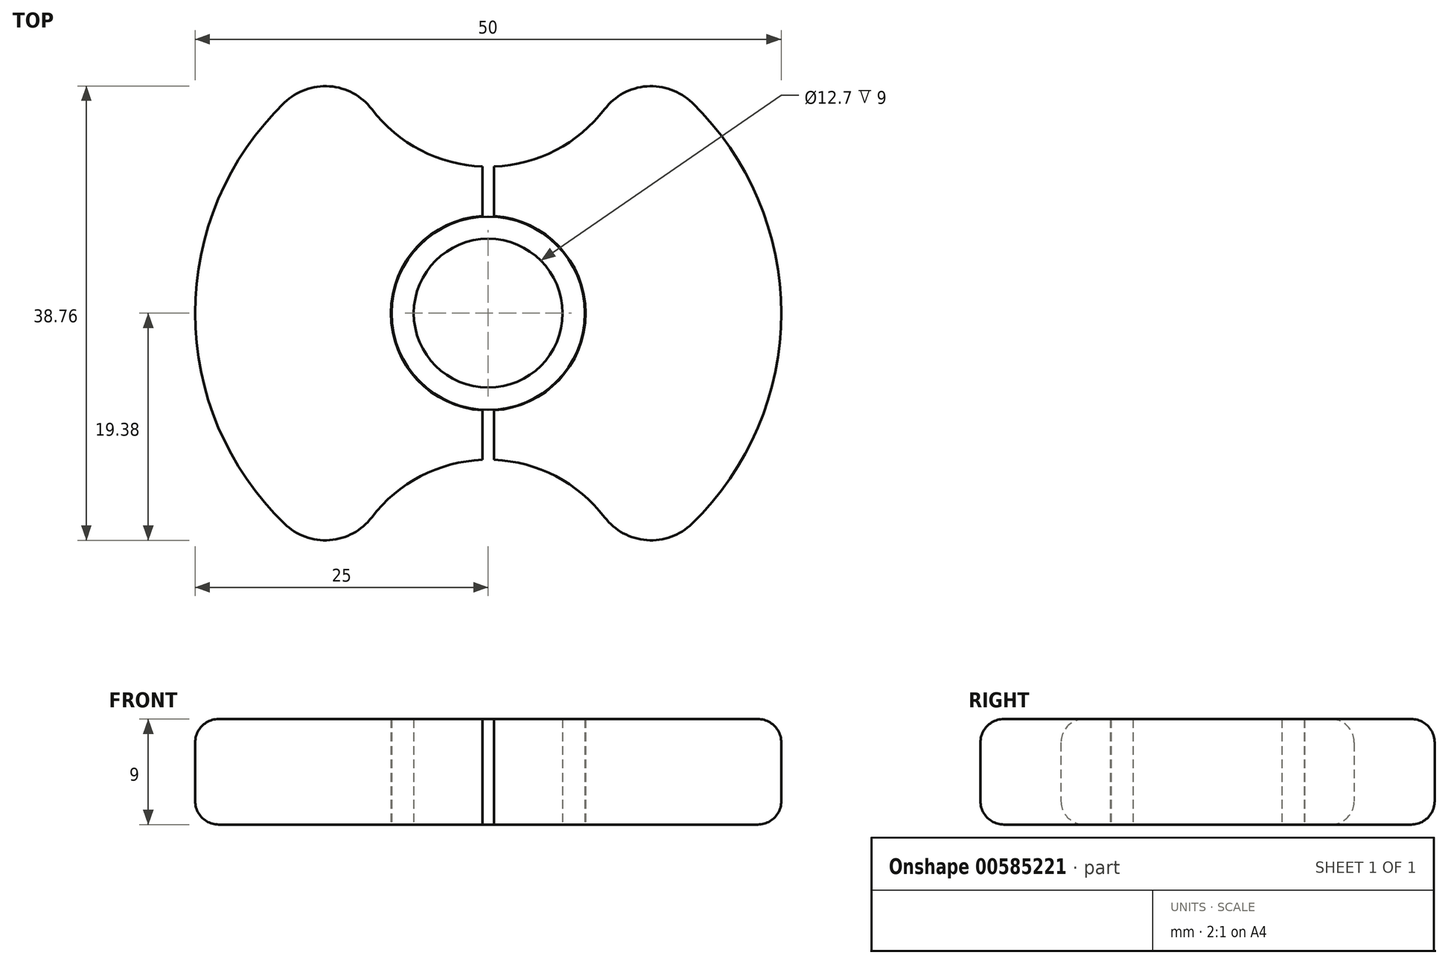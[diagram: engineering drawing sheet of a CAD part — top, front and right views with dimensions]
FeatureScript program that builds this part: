
annotation { "Feature Type Name" : "Feature", "Feature Type Description" : "" }
export const myFeature = defineFeature(function(context is Context, id is Id, definition is map)
    precondition{}
    {
        {
            var Q0;
            Q0=qCreatedBy(makeId("Top.planeOp"),FACE);
            var sketch = newSketch(context, id + "F0", { "sketchPlane" : qUnion([Q0])});
            skCircle(sketch, "E0", {"center": v(0, 0) * mm, "radius": 6.35 * mm});
            skArc(sketch, "E1", {"start": v(-12.1, 21.87) * mm, "mid": v(-25, 0) * mm, "end": v(-12.1, -21.88) * mm});
            skCircle(sketch, "E2", {"center": v(0, 0) * mm, "radius": 8.25 * mm});
            skArc(sketch, "E3", {"start": v(-12.1, 21.88) * mm, "mid": v(-7.85, 15.27) * mm, "end": v(-0.5, 12.51) * mm});
            skArc(sketch, "E4", {"start": v(12.1, -21.88) * mm, "mid": v(7.85, -15.27) * mm, "end": v(0.5, -12.51) * mm});
            skArc(sketch, "E5.trimOffspring", {"start": v(12.1, -21.88) * mm, "mid": v(25, 0) * mm, "end": v(12.1, 21.88) * mm});
            skArc(sketch, "E6", {"start": v(-0.5, 8.28) * mm, "mid": v(-8.3, 0) * mm, "end": v(-0.5, -8.28) * mm});
            skLineSegment(sketch, "E7.left", {"start": v(-0.5, -12.51) * mm, "end": v(-0.5, -8.28) * mm});
            skLineSegment(sketch, "E7.right", {"start": v(0.5, -12.51) * mm, "end": v(0.5, -8.28) * mm});
            skPoint(sketch, "E8.orphan", {"position": v(-0.5, 17.5) * mm});
            skPoint(sketch, "E9.orphan", {"position": v(0.5, 17.5) * mm});
            skArc(sketch, "E10.trimOffspring", {"start": v(0.5, 12.51) * mm, "mid": v(7.85, 15.27) * mm, "end": v(12.1, 21.88) * mm});
            skLineSegment(sketch, "E11.trimOffspring", {"start": v(0.5, 8.28) * mm, "end": v(0.5, 12.51) * mm});
            skLineSegment(sketch, "E12.trimOffspring", {"start": v(-0.5, 8.28) * mm, "end": v(-0.5, 12.51) * mm});
            skPoint(sketch, "E13.orphan", {"position": v(0.5, -17.5) * mm});
            skPoint(sketch, "E14.orphan", {"position": v(-0.5, -17.5) * mm});
            skArc(sketch, "E15.trimOffspring", {"start": v(-0.5, -12.51) * mm, "mid": v(-7.85, -15.27) * mm, "end": v(-12.1, -21.88) * mm});
            skArc(sketch, "E16.trimOffspring", {"start": v(0.5, -8.28) * mm, "mid": v(8.3, 0) * mm, "end": v(0.5, 8.28) * mm});
            skSolve(sketch);
        }
        {
            var Q0;
            Q0=makeQuery(id+"F0.imprint","IMPRINT",FACE,{"disambiguationData":[TD([[makeQuery(id+"F0.imprint","IMPRINT",EDGE,{"derivedFrom":sQuery(id+"F0.wireOp",EDGE,"E4")}),-1.0]])]});
            var Q1;
            Q1=makeQuery(id+"F0.imprint","IMPRINT",FACE,{"disambiguationData":[TD([[makeQuery(id+"F0.imprint","IMPRINT",EDGE,{"derivedFrom":sQuery(id+"F0.wireOp",EDGE,"E1")}),1.0]])]});
            var Q2;
            Q2=makeQuery(id+"F0.imprint","IMPRINT",FACE,{"disambiguationData":[TD([[makeQuery(id+"F0.imprint","IMPRINT",EDGE,{"derivedFrom":sQuery(id+"F0.wireOp",EDGE,"E0")}),-1.0]])]});
            extrude(context, id + "F1", {"entities" : qUnion([Q0, Q1, Q2]), "depth" : 9 * mm, "offsetDistance" : 25 * mm});
        }
        {
            var Q0;
            Q0=makeQuery(id+"F1.opExtrude","CAP_EDGE",EDGE,{"disambiguationData":[OSD([sQuery(id+"F0.wireOp",EDGE,"E4")])],"isStart":false});
            var Q1;
            Q1=makeQuery(id+"F1.opExtrude","CAP_EDGE",EDGE,{"disambiguationData":[OSD([sQuery(id+"F0.wireOp",EDGE,"E5.trimOffspring")])],"isStart":false});
            var Q2;
            Q2=makeQuery(id+"F1.opExtrude","CAP_EDGE",EDGE,{"disambiguationData":[OSD([sQuery(id+"F0.wireOp",EDGE,"E10.trimOffspring")])],"isStart":false});
            fillet(context, id + "F2", {"entities" : qUnion([Q0, Q1, Q2]), "radius" : 2 * mm, "tangentPropagation" : true, "allowEdgeOverflow" : false});
        }
        {
            var Q0;
            Q0=makeQuery(id+"F1.opExtrude","CAP_EDGE",EDGE,{"disambiguationData":[OSD([sQuery(id+"F0.wireOp",EDGE,"E3")])],"isStart":false});
            var Q1;
            Q1=makeQuery(id+"F1.opExtrude","CAP_EDGE",EDGE,{"disambiguationData":[OSD([sQuery(id+"F0.wireOp",EDGE,"E1")])],"isStart":false});
            var Q2;
            Q2=makeQuery(id+"F1.opExtrude","CAP_EDGE",EDGE,{"disambiguationData":[OSD([sQuery(id+"F0.wireOp",EDGE,"E15.trimOffspring")])],"isStart":false});
            fillet(context, id + "F3", {"entities" : qUnion([Q0, Q1, Q2]), "radius" : 2 * mm, "tangentPropagation" : true, "allowEdgeOverflow" : false});
        }
        {
            var Q0;
            Q0=makeQuery(id+"F2.opFillet","BLEND_EDGE",EDGE,{"blendedFrom":[makeQuery(id+"F1.opExtrude","CAP_EDGE",EDGE,{"disambiguationData":[OSD([sQuery(id+"F0.wireOp",EDGE,"E4")])],"isStart":false}),makeQuery(id+"F1.opExtrude","CAP_EDGE",EDGE,{"disambiguationData":[OSD([sQuery(id+"F0.wireOp",EDGE,"E5.trimOffspring")])],"isStart":false})],"blendedInto":[]});
            fillet(context, id + "F4", {"entities" : qUnion([Q0]), "radius" : 5 * mm, "tangentPropagation" : true, "allowEdgeOverflow" : false});
        }
        {
            var Q0;
            Q0=makeQuery(id+"F2.opFillet","BLEND_EDGE",EDGE,{"blendedFrom":[makeQuery(id+"F1.opExtrude","CAP_EDGE",EDGE,{"disambiguationData":[OSD([sQuery(id+"F0.wireOp",EDGE,"E5.trimOffspring")])],"isStart":false}),makeQuery(id+"F1.opExtrude","CAP_EDGE",EDGE,{"disambiguationData":[OSD([sQuery(id+"F0.wireOp",EDGE,"E10.trimOffspring")])],"isStart":false})],"blendedInto":[]});
            fillet(context, id + "F5", {"entities" : qUnion([Q0]), "radius" : 5 * mm, "tangentPropagation" : true, "allowEdgeOverflow" : false});
        }
        {
            var Q0;
            Q0=makeQuery(id+"F3.opFillet","BLEND_EDGE",EDGE,{"blendedFrom":[makeQuery(id+"F1.opExtrude","CAP_EDGE",EDGE,{"disambiguationData":[OSD([sQuery(id+"F0.wireOp",EDGE,"E1")])],"isStart":false}),makeQuery(id+"F1.opExtrude","CAP_EDGE",EDGE,{"disambiguationData":[OSD([sQuery(id+"F0.wireOp",EDGE,"E3")])],"isStart":false})],"blendedInto":[]});
            fillet(context, id + "F6", {"entities" : qUnion([Q0]), "radius" : 5 * mm, "tangentPropagation" : true, "allowEdgeOverflow" : false});
        }
        {
            var Q0;
            Q0=makeQuery(id+"F3.opFillet","BLEND_EDGE",EDGE,{"blendedFrom":[makeQuery(id+"F1.opExtrude","CAP_EDGE",EDGE,{"disambiguationData":[OSD([sQuery(id+"F0.wireOp",EDGE,"E1")])],"isStart":false}),makeQuery(id+"F1.opExtrude","CAP_EDGE",EDGE,{"disambiguationData":[OSD([sQuery(id+"F0.wireOp",EDGE,"E15.trimOffspring")])],"isStart":false})],"blendedInto":[]});
            fillet(context, id + "F7", {"entities" : qUnion([Q0]), "radius" : 5 * mm, "tangentPropagation" : true, "allowEdgeOverflow" : false});
        }
        {
            var Q0;
            Q0=makeQuery(id+"F1.opExtrude","CAP_EDGE",EDGE,{"disambiguationData":[OSD([sQuery(id+"F0.wireOp",EDGE,"E5.trimOffspring")])],"isStart":true});
            var Q1;
            {var subQ0=sQuery(id+"F0.wireOp",EDGE,"E5.trimOffspring");var subQ1=sQuery(id+"F0.wireOp",EDGE,"E4");Q1=makeQuery(id+"F4.opFillet","BLEND_EDGE",EDGE,{"blendedFrom":[makeQuery(id+"F1.opExtrude","SWEPT_EDGE",EDGE,{"disambiguationData":[OSD([subQ1,subQ0])]}),makeQuery(id+"F1.opExtrude","CAP_FACE",FACE,{"disambiguationData":[OSD([subQ1,subQ0,sQuery(id+"F0.wireOp",EDGE,"E7.right"),sQuery(id+"F0.wireOp",EDGE,"E10.trimOffspring"),sQuery(id+"F0.wireOp",EDGE,"E11.trimOffspring"),sQuery(id+"F0.wireOp",EDGE,"E16.trimOffspring")])],"isStart":true})],"blendedInto":[makeQuery(id+"F1.opExtrude","CAP_FACE",FACE,{"disambiguationData":[OSD([subQ1,subQ0,sQuery(id+"F0.wireOp",EDGE,"E7.right"),sQuery(id+"F0.wireOp",EDGE,"E10.trimOffspring"),sQuery(id+"F0.wireOp",EDGE,"E11.trimOffspring"),sQuery(id+"F0.wireOp",EDGE,"E16.trimOffspring")])],"isStart":true})]});}
            var Q2;
            Q2=makeQuery(id+"F1.opExtrude","CAP_EDGE",EDGE,{"disambiguationData":[OSD([sQuery(id+"F0.wireOp",EDGE,"E4")])],"isStart":true});
            var Q3;
            Q3=makeQuery(id+"F1.opExtrude","CAP_EDGE",EDGE,{"disambiguationData":[OSD([sQuery(id+"F0.wireOp",EDGE,"E10.trimOffspring")])],"isStart":true});
            var Q4;
            {var subQ0=sQuery(id+"F0.wireOp",EDGE,"E10.trimOffspring");var subQ1=sQuery(id+"F0.wireOp",EDGE,"E5.trimOffspring");Q4=makeQuery(id+"F5.opFillet","BLEND_EDGE",EDGE,{"blendedFrom":[makeQuery(id+"F1.opExtrude","SWEPT_EDGE",EDGE,{"disambiguationData":[OSD([subQ1,subQ0])]}),makeQuery(id+"F1.opExtrude","CAP_FACE",FACE,{"disambiguationData":[OSD([sQuery(id+"F0.wireOp",EDGE,"E4"),subQ1,sQuery(id+"F0.wireOp",EDGE,"E7.right"),subQ0,sQuery(id+"F0.wireOp",EDGE,"E11.trimOffspring"),sQuery(id+"F0.wireOp",EDGE,"E16.trimOffspring")])],"isStart":true})],"blendedInto":[makeQuery(id+"F1.opExtrude","CAP_FACE",FACE,{"disambiguationData":[OSD([sQuery(id+"F0.wireOp",EDGE,"E4"),subQ1,sQuery(id+"F0.wireOp",EDGE,"E7.right"),subQ0,sQuery(id+"F0.wireOp",EDGE,"E11.trimOffspring"),sQuery(id+"F0.wireOp",EDGE,"E16.trimOffspring")])],"isStart":true})]});}
            fillet(context, id + "F8", {"entities" : qUnion([Q0, Q1, Q2, Q3, Q4]), "radius" : 2 * mm, "tangentPropagation" : true, "allowEdgeOverflow" : false});
        }
        {
            var Q0;
            Q0=makeQuery(id+"F1.opExtrude","CAP_EDGE",EDGE,{"disambiguationData":[OSD([sQuery(id+"F0.wireOp",EDGE,"E3")])],"isStart":true});
            var Q1;
            {var subQ0=sQuery(id+"F0.wireOp",EDGE,"E3");var subQ1=sQuery(id+"F0.wireOp",EDGE,"E1");Q1=makeQuery(id+"F6.opFillet","BLEND_EDGE",EDGE,{"blendedFrom":[makeQuery(id+"F1.opExtrude","SWEPT_EDGE",EDGE,{"disambiguationData":[OSD([subQ1,subQ0])]}),makeQuery(id+"F1.opExtrude","CAP_FACE",FACE,{"disambiguationData":[OSD([subQ1,subQ0,sQuery(id+"F0.wireOp",EDGE,"E6"),sQuery(id+"F0.wireOp",EDGE,"E7.left"),sQuery(id+"F0.wireOp",EDGE,"E12.trimOffspring"),sQuery(id+"F0.wireOp",EDGE,"E15.trimOffspring")])],"isStart":true})],"blendedInto":[makeQuery(id+"F1.opExtrude","CAP_FACE",FACE,{"disambiguationData":[OSD([subQ1,subQ0,sQuery(id+"F0.wireOp",EDGE,"E6"),sQuery(id+"F0.wireOp",EDGE,"E7.left"),sQuery(id+"F0.wireOp",EDGE,"E12.trimOffspring"),sQuery(id+"F0.wireOp",EDGE,"E15.trimOffspring")])],"isStart":true})]});}
            var Q2;
            Q2=makeQuery(id+"F1.opExtrude","CAP_EDGE",EDGE,{"disambiguationData":[OSD([sQuery(id+"F0.wireOp",EDGE,"E1")])],"isStart":true});
            var Q3;
            {var subQ0=sQuery(id+"F0.wireOp",EDGE,"E15.trimOffspring");var subQ1=sQuery(id+"F0.wireOp",EDGE,"E1");Q3=makeQuery(id+"F7.opFillet","BLEND_EDGE",EDGE,{"blendedFrom":[makeQuery(id+"F1.opExtrude","SWEPT_EDGE",EDGE,{"disambiguationData":[OSD([subQ1,subQ0])]}),makeQuery(id+"F1.opExtrude","CAP_FACE",FACE,{"disambiguationData":[OSD([subQ1,sQuery(id+"F0.wireOp",EDGE,"E3"),sQuery(id+"F0.wireOp",EDGE,"E6"),sQuery(id+"F0.wireOp",EDGE,"E7.left"),sQuery(id+"F0.wireOp",EDGE,"E12.trimOffspring"),subQ0])],"isStart":true})],"blendedInto":[makeQuery(id+"F1.opExtrude","CAP_FACE",FACE,{"disambiguationData":[OSD([subQ1,sQuery(id+"F0.wireOp",EDGE,"E3"),sQuery(id+"F0.wireOp",EDGE,"E6"),sQuery(id+"F0.wireOp",EDGE,"E7.left"),sQuery(id+"F0.wireOp",EDGE,"E12.trimOffspring"),subQ0])],"isStart":true})]});}
            var Q4;
            Q4=makeQuery(id+"F1.opExtrude","CAP_EDGE",EDGE,{"disambiguationData":[OSD([sQuery(id+"F0.wireOp",EDGE,"E15.trimOffspring")])],"isStart":true});
            fillet(context, id + "F9", {"entities" : qUnion([Q0, Q1, Q2, Q3, Q4]), "radius" : 2 * mm, "tangentPropagation" : true, "allowEdgeOverflow" : false});
        }
    });
